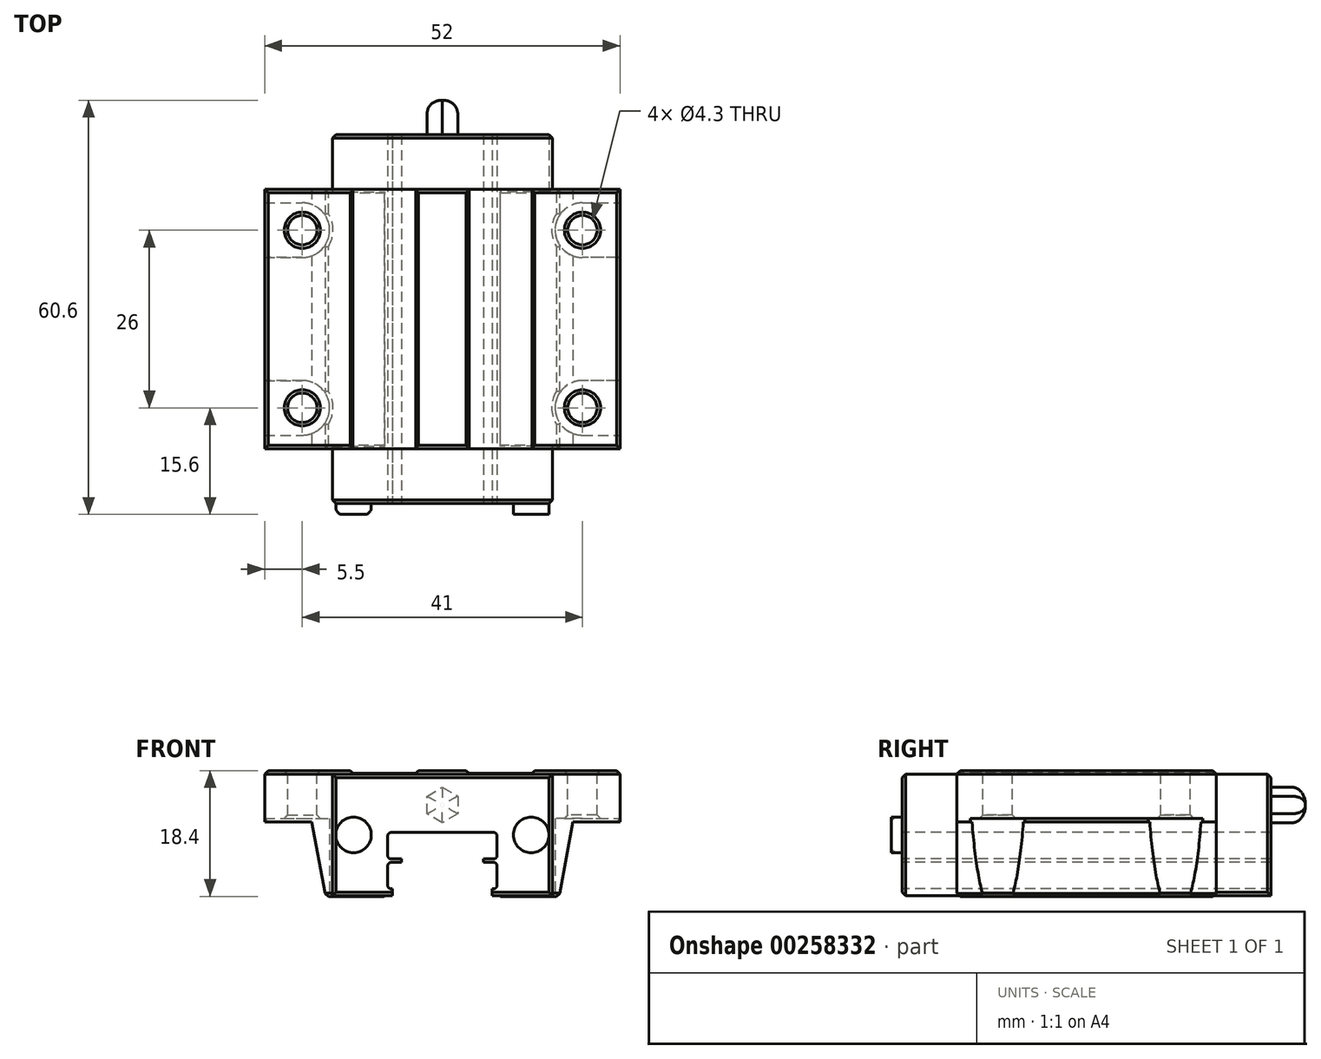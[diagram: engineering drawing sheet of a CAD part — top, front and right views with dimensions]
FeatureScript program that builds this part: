
annotation { "Feature Type Name" : "Feature", "Feature Type Description" : "" }
export const myFeature = defineFeature(function(context is Context, id is Id, definition is map)
    precondition{}
    {
        {
            var Q0;
            Q0=qCreatedBy(makeId("Front.planeOp"),FACE);
            var sketch = newSketch(context, id + "F0", { "sketchPlane" : qUnion([Q0])});
            skLineSegment(sketch, "E0", {"start": v(0, 7.25) * mm, "end": v(0, -7.25) * mm, "construction": true});
            skLineSegment(sketch, "E1", {"start": v(0, -7.25) * mm, "end": v(-7.5, -7.25) * mm});
            skLineSegment(sketch, "E2", {"start": v(-7.5, -7.25) * mm, "end": v(-7.5, -4.13) * mm});
            skLineSegment(sketch, "E3", {"start": v(-7.5, -4.13) * mm, "end": v(-7.5, -4.13) * mm});
            skLineSegment(sketch, "E4", {"start": v(-6.8, -3.43) * mm, "end": v(-6.8, -0.7) * mm});
            skLineSegment(sketch, "E5", {"start": v(-7.5, 0) * mm, "end": v(-7.5, 0) * mm});
            skLineSegment(sketch, "E6", {"start": v(-7.5, 0) * mm, "end": v(-7.5, 1.88) * mm});
            skLineSegment(sketch, "E7", {"start": v(-7.5, 1.88) * mm, "end": v(-7.5, 1.88) * mm});
            skLineSegment(sketch, "E8", {"start": v(-6.8, 2.88) * mm, "end": v(-5.5, 2.88) * mm});
            skLineSegment(sketch, "E9", {"start": v(-5.5, 2.88) * mm, "end": v(-5.5, 4.38) * mm});
            skLineSegment(sketch, "E10", {"start": v(-5.5, 4.38) * mm, "end": v(-6.8, 4.38) * mm});
            skLineSegment(sketch, "E11", {"start": v(-6.8, 4.38) * mm, "end": v(-6.8, 4.68) * mm});
            skLineSegment(sketch, "E12", {"start": v(-7.5, 5.38) * mm, "end": v(-7.5, 5.38) * mm});
            skLineSegment(sketch, "E13", {"start": v(-7.5, 5.38) * mm, "end": v(-7.5, 7.25) * mm});
            skLineSegment(sketch, "E14", {"start": v(-7.5, 7.25) * mm, "end": v(0, 7.25) * mm});
            skLineSegment(sketch, "E15", {"start": v(-6.8, 2.58) * mm, "end": v(-6.8, 2.87) * mm});
            skPoint(sketch, "E16.visualSharp", {"position": v(-6.8, -4.13) * mm});
            skArc(sketch, "E16.filletArc", {"start": v(-7.5, -4.13) * mm, "mid": v(-7, -3.92) * mm, "end": v(-6.8, -3.43) * mm});
            skPoint(sketch, "E17.visualSharp", {"position": v(-6.8, 0) * mm});
            skArc(sketch, "E17.filletArc", {"start": v(-6.8, -0.7) * mm, "mid": v(-7, -0.2) * mm, "end": v(-7.5, 0) * mm});
            skPoint(sketch, "E18.visualSharp", {"position": v(-6.8, 1.88) * mm});
            skArc(sketch, "E18.filletArc", {"start": v(-7.5, 1.88) * mm, "mid": v(-7, 2.08) * mm, "end": v(-6.8, 2.58) * mm});
            skPoint(sketch, "E19.visualSharp", {"position": v(-6.8, 5.38) * mm});
            skArc(sketch, "E19.filletArc", {"start": v(-6.8, 4.68) * mm, "mid": v(-7, 5.17) * mm, "end": v(-7.5, 5.38) * mm});
            skLineSegment(sketch, "E20.MirrorCS", {"start": v(6.8, 2.58) * mm, "end": v(6.8, 2.87) * mm});
            skLineSegment(sketch, "E21.MirrorCS", {"start": v(6.8, 4.38) * mm, "end": v(6.8, 4.68) * mm});
            skArc(sketch, "E22.MirrorCS", {"start": v(6.8, 4.68) * mm, "mid": v(7, 5.17) * mm, "end": v(7.5, 5.38) * mm});
            skArc(sketch, "E23.MirrorCS", {"start": v(7.5, 1.88) * mm, "mid": v(7, 2.08) * mm, "end": v(6.8, 2.58) * mm});
            skArc(sketch, "E24.MirrorCS", {"start": v(7.5, -4.13) * mm, "mid": v(7, -3.92) * mm, "end": v(6.8, -3.43) * mm});
            skArc(sketch, "E25.MirrorCS", {"start": v(6.8, -0.7) * mm, "mid": v(7, -0.2) * mm, "end": v(7.5, 0) * mm});
            skLineSegment(sketch, "E26.MirrorCS", {"start": v(7.5, 0) * mm, "end": v(7.5, 0) * mm});
            skLineSegment(sketch, "E27.MirrorCS", {"start": v(7.5, -7.25) * mm, "end": v(7.5, -4.13) * mm});
            skPoint(sketch, "E28.MirrorP", {"position": v(6.8, 0) * mm});
            skPoint(sketch, "E29.MirrorP", {"position": v(6.8, 5.38) * mm});
            skPoint(sketch, "E30.MirrorP", {"position": v(6.8, 1.88) * mm});
            skLineSegment(sketch, "E31.MirrorCS", {"start": v(7.5, -4.13) * mm, "end": v(7.5, -4.13) * mm});
            skLineSegment(sketch, "E32.MirrorCS", {"start": v(7.5, 1.88) * mm, "end": v(7.5, 1.88) * mm});
            skLineSegment(sketch, "E33.MirrorCS", {"start": v(7.5, 5.38) * mm, "end": v(7.5, 5.38) * mm});
            skLineSegment(sketch, "E34.MirrorCS", {"start": v(7.5, 5.38) * mm, "end": v(7.5, 7.25) * mm});
            skLineSegment(sketch, "E35.MirrorCS", {"start": v(5.5, 4.38) * mm, "end": v(6.8, 4.38) * mm});
            skLineSegment(sketch, "E36.MirrorCS", {"start": v(6.8, -3.43) * mm, "end": v(6.8, -0.7) * mm});
            skPoint(sketch, "E37.MirrorP", {"position": v(6.8, -4.13) * mm});
            skLineSegment(sketch, "E38.MirrorCS", {"start": v(6.8, 2.88) * mm, "end": v(5.5, 2.88) * mm});
            skLineSegment(sketch, "E39.MirrorCS", {"start": v(7.5, 0) * mm, "end": v(7.5, 1.88) * mm});
            skLineSegment(sketch, "E40.MirrorCS", {"start": v(5.5, 2.88) * mm, "end": v(5.5, 4.38) * mm});
            skLineSegment(sketch, "E41.MirrorCS", {"start": v(7.5, 7.25) * mm, "end": v(0, 7.25) * mm});
            skLineSegment(sketch, "E42.MirrorCS", {"start": v(0, -7.25) * mm, "end": v(7.5, -7.25) * mm});
            skSolve(sketch);
        }
        {
            var Q0;
            Q0=qCreatedBy(makeId("Front.planeOp"),FACE);
            var sketch = newSketch(context, id + "F1", { "sketchPlane" : qUnion([Q0])});
            skLineSegment(sketch, "E43", {"start": v(-16.1, 16.3) * mm, "end": v(-16.1, -1.5) * mm});
            skLineSegment(sketch, "E44", {"start": v(-16.1, -1.5) * mm, "end": v(-7.3, -1.5) * mm});
            skLineSegment(sketch, "E45", {"start": v(-7.3, -1.5) * mm, "end": v(-7.3, -0.5) * mm});
            skLineSegment(sketch, "E46", {"start": v(-7.3, -0.5) * mm, "end": v(-7.5, -0.5) * mm});
            skLineSegment(sketch, "E47", {"start": v(-8, 0) * mm, "end": v(-8, 2.88) * mm});
            skLineSegment(sketch, "E48", {"start": v(-7.5, 3.38) * mm, "end": v(-6, 3.38) * mm});
            skLineSegment(sketch, "E49", {"start": v(-6, 3.38) * mm, "end": v(-6, 3.88) * mm});
            skLineSegment(sketch, "E50", {"start": v(-6, 3.88) * mm, "end": v(-7.5, 3.88) * mm});
            skLineSegment(sketch, "E51", {"start": v(-8, 4.38) * mm, "end": v(-8, 7.25) * mm});
            skLineSegment(sketch, "E52", {"start": v(-7.5, 7.75) * mm, "end": v(0, 7.75) * mm});
            skLineSegment(sketch, "E53", {"start": v(-16.1, 16.3) * mm, "end": v(0, 16.3) * mm});
            skLineSegment(sketch, "E54", {"start": v(0, 16.3) * mm, "end": v(0, 0) * mm, "construction": true});
            skPoint(sketch, "E55.visualSharp", {"position": v(-8, 7.75) * mm});
            skArc(sketch, "E55.filletArc", {"start": v(-7.5, 7.75) * mm, "mid": v(-7.85, 7.6) * mm, "end": v(-8, 7.25) * mm});
            skPoint(sketch, "E56.visualSharp", {"position": v(-8, 3.88) * mm});
            skArc(sketch, "E56.filletArc", {"start": v(-8, 4.38) * mm, "mid": v(-7.85, 4.02) * mm, "end": v(-7.5, 3.88) * mm});
            skPoint(sketch, "E57.visualSharp", {"position": v(-8, 3.38) * mm});
            skArc(sketch, "E57.filletArc", {"start": v(-7.5, 3.38) * mm, "mid": v(-7.85, 3.23) * mm, "end": v(-8, 2.88) * mm});
            skPoint(sketch, "E58.visualSharp", {"position": v(-8, -0.5) * mm});
            skArc(sketch, "E58.filletArc", {"start": v(-8, 0) * mm, "mid": v(-7.85, -0.35) * mm, "end": v(-7.5, -0.5) * mm});
            skArc(sketch, "E59.MirrorCS", {"start": v(7.5, 7.75) * mm, "mid": v(7.85, 7.6) * mm, "end": v(8, 7.25) * mm});
            skArc(sketch, "E60.MirrorCS", {"start": v(7.5, 3.38) * mm, "mid": v(7.85, 3.23) * mm, "end": v(8, 2.88) * mm});
            skArc(sketch, "E61.MirrorCS", {"start": v(8, 0) * mm, "mid": v(7.85, -0.35) * mm, "end": v(7.5, -0.5) * mm});
            skLineSegment(sketch, "E62.MirrorCS", {"start": v(7.3, -0.5) * mm, "end": v(7.5, -0.5) * mm});
            skArc(sketch, "E63.MirrorCS", {"start": v(8, 4.38) * mm, "mid": v(7.85, 4.02) * mm, "end": v(7.5, 3.88) * mm});
            skLineSegment(sketch, "E64.MirrorCS", {"start": v(6, 3.88) * mm, "end": v(7.5, 3.88) * mm});
            skLineSegment(sketch, "E65.MirrorCS", {"start": v(8, 4.38) * mm, "end": v(8, 7.25) * mm});
            skLineSegment(sketch, "E66.MirrorCS", {"start": v(7.5, 3.38) * mm, "end": v(6, 3.38) * mm});
            skLineSegment(sketch, "E67.MirrorCS", {"start": v(7.3, -1.5) * mm, "end": v(7.3, -0.5) * mm});
            skLineSegment(sketch, "E68.MirrorCS", {"start": v(8, 0) * mm, "end": v(8, 2.88) * mm});
            skLineSegment(sketch, "E69.MirrorCS", {"start": v(6, 3.38) * mm, "end": v(6, 3.88) * mm});
            skPoint(sketch, "E70.MirrorP", {"position": v(8, 3.38) * mm});
            skPoint(sketch, "E71.MirrorP", {"position": v(8, 3.88) * mm});
            skLineSegment(sketch, "E72.MirrorCS", {"start": v(7.5, 7.75) * mm, "end": v(0, 7.75) * mm});
            skPoint(sketch, "E73.MirrorP", {"position": v(8, -0.5) * mm});
            skLineSegment(sketch, "E74.MirrorCS", {"start": v(16.1, 16.3) * mm, "end": v(0, 16.3) * mm});
            skLineSegment(sketch, "E75.MirrorCS", {"start": v(16.1, 16.3) * mm, "end": v(16.1, -1.5) * mm});
            skLineSegment(sketch, "E76.MirrorCS", {"start": v(16.1, -1.5) * mm, "end": v(7.3, -1.5) * mm});
            skPoint(sketch, "E77.MirrorP", {"position": v(8, 7.75) * mm});
            skSolve(sketch);
        }
        {
            var Q0;
            Q0=qSketchRegion(id+"F1",true);
            extrude(context, id + "F2", {"entities" : qUnion([Q0]), "oppositeDirection" : true, "depth" : 54 * mm});
        }
        {
            var Q0;
            Q0=qCreatedBy(makeId("Front.planeOp"),FACE);
            cPlane(context, id + "F3", {"entities" : qUnion([Q0]), "cplaneType" : CPlaneType.OFFSET, "offset" : 8 * mm, "oppositeDirection" : true, "width" : 150 * mm, "height" : 150 * mm});
        }
        {
            var Q0;
            Q0=qCreatedBy(id+"F3.planeOp",FACE);
            var sketch = newSketch(context, id + "F4", { "sketchPlane" : qUnion([Q0])});
            skLineSegment(sketch, "E78", {"start": v(-8, -1.6) * mm, "end": v(-17.1, -1.6) * mm});
            skLineSegment(sketch, "E79", {"start": v(-17.1, -1.6) * mm, "end": v(-19.1, 9.3) * mm});
            skLineSegment(sketch, "E80", {"start": v(-19.1, 9.3) * mm, "end": v(-26, 9.3) * mm});
            skLineSegment(sketch, "E81", {"start": v(-26, 9.3) * mm, "end": v(-26, 16.8) * mm});
            skLineSegment(sketch, "E82", {"start": v(0, 16.8) * mm, "end": v(0, 0) * mm, "construction": true});
            skLineSegment(sketch, "E83", {"start": v(-26, 16.8) * mm, "end": v(-13, 16.8) * mm});
            skLineSegment(sketch, "E84", {"start": v(-13, 16.8) * mm, "end": v(-13, 16.4) * mm});
            skLineSegment(sketch, "E85", {"start": v(-13, 16.4) * mm, "end": v(-4, 16.4) * mm});
            skLineSegment(sketch, "E86", {"start": v(-4, 16.4) * mm, "end": v(-4, 16.8) * mm});
            skLineSegment(sketch, "E87", {"start": v(-4, 16.8) * mm, "end": v(0, 16.8) * mm});
            skLineSegment(sketch, "E88", {"start": v(-8, -1.6) * mm, "end": v(-8, 7.75) * mm});
            skLineSegment(sketch, "E89", {"start": v(-8, 7.75) * mm, "end": v(0, 7.75) * mm});
            skLineSegment(sketch, "E90.MirrorCS", {"start": v(4, 16.4) * mm, "end": v(4, 16.8) * mm});
            skLineSegment(sketch, "E91.MirrorCS", {"start": v(13, 16.8) * mm, "end": v(13, 16.4) * mm});
            skLineSegment(sketch, "E92.MirrorCS", {"start": v(8, -1.6) * mm, "end": v(8, 7.75) * mm});
            skLineSegment(sketch, "E93.MirrorCS", {"start": v(4, 16.8) * mm, "end": v(0, 16.8) * mm});
            skLineSegment(sketch, "E94.MirrorCS", {"start": v(26, 16.8) * mm, "end": v(13, 16.8) * mm});
            skLineSegment(sketch, "E95.MirrorCS", {"start": v(26, 9.3) * mm, "end": v(26, 16.8) * mm});
            skLineSegment(sketch, "E96.MirrorCS", {"start": v(8, -1.6) * mm, "end": v(17.1, -1.6) * mm});
            skLineSegment(sketch, "E97.MirrorCS", {"start": v(17.1, -1.6) * mm, "end": v(19.1, 9.3) * mm});
            skLineSegment(sketch, "E98.MirrorCS", {"start": v(8, 7.75) * mm, "end": v(0, 7.75) * mm});
            skLineSegment(sketch, "E99.MirrorCS", {"start": v(19.1, 9.3) * mm, "end": v(26, 9.3) * mm});
            skLineSegment(sketch, "E100.MirrorCS", {"start": v(13, 16.4) * mm, "end": v(4, 16.4) * mm});
            skSolve(sketch);
        }
        {
            var Q0;
            Q0=qSketchRegion(id+"F4",true);
            extrude(context, id + "F5", {"entities" : qUnion([Q0]), "operationType" : NewBodyOperationType.ADD, "oppositeDirection" : true, "depth" : 38 * mm});
        }
        {
            var Q0;
            Q0=makeQuery(id+"F5.opExtrude","SWEPT_FACE",FACE,{"disambiguationData":[OSD([sQuery(id+"F4.wireOp",EDGE,"E83")])]});
            var sketch = newSketch(context, id + "F6", { "sketchPlane" : qUnion([Q0])});
            skCircle(sketch, "E101", {"center": v(-20.5, 40) * mm, "radius": 2.15 * mm});
            skCircle(sketch, "E102", {"center": v(-20.5, 14) * mm, "radius": 2.15 * mm});
            skLineSegment(sketch, "E103", {"start": v(-26, 27) * mm, "end": v(-13, 27) * mm, "construction": true});
            skCircle(sketch, "E104.MirrorC", {"center": v(20.5, 40) * mm, "radius": 2.15 * mm});
            skCircle(sketch, "E105.MirrorC", {"center": v(20.5, 14) * mm, "radius": 2.15 * mm});
            skSolve(sketch);
        }
        {
            var Q0;
            Q0=qSketchRegion(id+"F6",true);
            extrude(context, id + "F7", {"entities" : qUnion([Q0]), "operationType" : NewBodyOperationType.REMOVE, "endBound" : BoundingType.THROUGH_ALL, "oppositeDirection" : true, "depth" : 25 * mm});
        }
        {
            var Q0;
            Q0=makeQuery(id+"F5.opExtrude","SWEPT_FACE",FACE,{"disambiguationData":[OSD([sQuery(id+"F4.wireOp",EDGE,"E80")])]});
            var sketch = newSketch(context, id + "F8", { "sketchPlane" : qUnion([Q0])});
            skArc(sketch, "E106", {"start": v(-20.5, -18) * mm, "mid": v(-16.5, -14) * mm, "end": v(-20.5, -10) * mm});
            skLineSegment(sketch, "E107", {"start": v(-26, -27) * mm, "end": v(-19.1, -27) * mm, "construction": true});
            skLineSegment(sketch, "E108", {"start": v(-20.5, -10) * mm, "end": v(-26, -10) * mm});
            skLineSegment(sketch, "E109", {"start": v(-26, -10) * mm, "end": v(-26, -18) * mm});
            skLineSegment(sketch, "E110", {"start": v(-26, -18) * mm, "end": v(-20.5, -18) * mm});
            skLineSegment(sketch, "E111.MirrorCS", {"start": v(-26, -36) * mm, "end": v(-20.5, -36) * mm});
            skLineSegment(sketch, "E112.MirrorCS", {"start": v(-26, -44) * mm, "end": v(-26, -36) * mm});
            skLineSegment(sketch, "E113.MirrorCS", {"start": v(-20.5, -44) * mm, "end": v(-26, -44) * mm});
            skArc(sketch, "E114.MirrorCS", {"start": v(-20.5, -36) * mm, "mid": v(-16.5, -40) * mm, "end": v(-20.5, -44) * mm});
            skArc(sketch, "E115.MirrorCS", {"start": v(20.5, -18) * mm, "mid": v(16.5, -14) * mm, "end": v(20.5, -10) * mm});
            skLineSegment(sketch, "E116.MirrorCS", {"start": v(26, -18) * mm, "end": v(20.5, -18) * mm});
            skLineSegment(sketch, "E117.MirrorCS", {"start": v(26, -10) * mm, "end": v(26, -18) * mm});
            skLineSegment(sketch, "E118.MirrorCS", {"start": v(20.5, -10) * mm, "end": v(26, -10) * mm});
            skLineSegment(sketch, "E119.MirrorCS", {"start": v(26, -36) * mm, "end": v(20.5, -36) * mm});
            skArc(sketch, "E120.MirrorCS", {"start": v(20.5, -36) * mm, "mid": v(16.5, -40) * mm, "end": v(20.5, -44) * mm});
            skLineSegment(sketch, "E121.MirrorCS", {"start": v(20.5, -44) * mm, "end": v(26, -44) * mm});
            skLineSegment(sketch, "E122.MirrorCS", {"start": v(26, -44) * mm, "end": v(26, -36) * mm});
            skSolve(sketch);
        }
        {
            var Q0;
            Q0=qSketchRegion(id+"F8",true);
            extrude(context, id + "F9", {"entities" : qUnion([Q0]), "operationType" : NewBodyOperationType.REMOVE, "oppositeDirection" : true, "depth" : 0.5 * mm, "hasSecondDirection" : true, "secondDirectionBound" : BoundingType.THROUGH_ALL, "secondDirectionOppositeDirection" : false, "secondDirectionDepth" : 25 * mm});
        }
        {
            var Q0;
            Q0=makeQuery(id+"F5.opExtrude","SWEPT_FACE",FACE,{"disambiguationData":[OSD([sQuery(id+"F4.wireOp",EDGE,"E78")])]});
            var Q1;
            Q1=makeQuery(id+"F5.opExtrude","SWEPT_FACE",FACE,{"disambiguationData":[OSD([sQuery(id+"F4.wireOp",EDGE,"E96.MirrorCS")])]});
            var Q2;
            Q2=makeQuery(id+"F7.boolean.opBoolean","COPY",FACE,{"derivedFrom":makeQuery(id+"F7.opExtrude","SWEPT_FACE",FACE,{"disambiguationData":[OSD([sQuery(id+"F6.wireOp",EDGE,"E101")])]})});
            var Q3;
            Q3=makeQuery(id+"F7.boolean.opBoolean","COPY",FACE,{"derivedFrom":makeQuery(id+"F7.opExtrude","SWEPT_FACE",FACE,{"disambiguationData":[OSD([sQuery(id+"F6.wireOp",EDGE,"E102")])]})});
            var Q4;
            Q4=makeQuery(id+"F7.boolean.opBoolean","COPY",FACE,{"derivedFrom":makeQuery(id+"F7.opExtrude","SWEPT_FACE",FACE,{"disambiguationData":[OSD([sQuery(id+"F6.wireOp",EDGE,"E105.MirrorC")])]})});
            var Q5;
            Q5=makeQuery(id+"F7.boolean.opBoolean","COPY",FACE,{"derivedFrom":makeQuery(id+"F7.opExtrude","SWEPT_FACE",FACE,{"disambiguationData":[OSD([sQuery(id+"F6.wireOp",EDGE,"E104.MirrorC")])]})});
            var Q6;
            Q6=makeQuery(id+"F5.opExtrude","SWEPT_FACE",FACE,{"disambiguationData":[OSD([sQuery(id+"F4.wireOp",EDGE,"E87"),sQuery(id+"F4.wireOp",EDGE,"E93.MirrorCS")])]});
            var Q7;
            Q7=makeQuery(id+"F5.opExtrude","SWEPT_FACE",FACE,{"disambiguationData":[OSD([sQuery(id+"F4.wireOp",EDGE,"E94.MirrorCS")])]});
            var Q8;
            Q8=makeQuery(id+"F5.opExtrude","SWEPT_FACE",FACE,{"disambiguationData":[OSD([sQuery(id+"F4.wireOp",EDGE,"E83")])]});
            chamfer(context, id + "F10", {"entities" : qUnion([Q0, Q1, Q2, Q3, Q4, Q5, Q6, Q7, Q8]), "width" : 0.5 * mm, "tangentPropagation" : true});
        }
        {
            var Q0;
            {var subQ0=sQuery(id+"F4.wireOp",EDGE,"E95.MirrorCS");var subQ1=sQuery(id+"F4.wireOp",EDGE,"E99.MirrorCS");Q0=makeQuery(id+"F9.boolean.opBoolean","SPLIT",EDGE,{"disambiguationData":[TD([makeQuery(id+"F9.opExtrude","SWEPT_FACE",FACE,{"disambiguationData":[OSD([sQuery(id+"F8.wireOp",EDGE,"E116.MirrorCS")])]})])],"derivedFrom":makeQuery(id+"F5.opExtrude","SWEPT_EDGE",EDGE,{"disambiguationData":[OSD([subQ0,subQ1])]})});}
            var Q1;
            {var subQ0=sQuery(id+"F1.wireOp",EDGE,"E76.MirrorCS");var subQ1=sQuery(id+"F1.wireOp",EDGE,"E75.MirrorCS");Q1=makeQuery(id+"F5.boolean.opBoolean","SPLIT",EDGE,{"disambiguationData":[TD([makeQuery(id+"F5.opExtrude","CAP_FACE",FACE,{"disambiguationData":[OSD([sQuery(id+"F4.wireOp",EDGE,"E78"),sQuery(id+"F4.wireOp",EDGE,"E79"),sQuery(id+"F4.wireOp",EDGE,"E80"),sQuery(id+"F4.wireOp",EDGE,"E81"),sQuery(id+"F4.wireOp",EDGE,"E83"),sQuery(id+"F4.wireOp",EDGE,"E84"),sQuery(id+"F4.wireOp",EDGE,"E85"),sQuery(id+"F4.wireOp",EDGE,"E86"),sQuery(id+"F4.wireOp",EDGE,"E87"),sQuery(id+"F4.wireOp",EDGE,"E88"),sQuery(id+"F4.wireOp",EDGE,"E89"),sQuery(id+"F4.wireOp",EDGE,"E90.MirrorCS"),sQuery(id+"F4.wireOp",EDGE,"E91.MirrorCS"),sQuery(id+"F4.wireOp",EDGE,"E92.MirrorCS"),sQuery(id+"F4.wireOp",EDGE,"E93.MirrorCS"),sQuery(id+"F4.wireOp",EDGE,"E94.MirrorCS"),sQuery(id+"F4.wireOp",EDGE,"E95.MirrorCS"),sQuery(id+"F4.wireOp",EDGE,"E96.MirrorCS"),sQuery(id+"F4.wireOp",EDGE,"E97.MirrorCS"),sQuery(id+"F4.wireOp",EDGE,"E98.MirrorCS"),sQuery(id+"F4.wireOp",EDGE,"E99.MirrorCS"),sQuery(id+"F4.wireOp",EDGE,"E100.MirrorCS")])],"isStart":false})])],"derivedFrom":makeQuery(id+"F2.opExtrude","SWEPT_EDGE",EDGE,{"disambiguationData":[OSD([subQ1,subQ0])]})});}
            var Q2;
            Q2=makeQuery(id+"F2.opExtrude","CAP_EDGE",EDGE,{"disambiguationData":[OSD([sQuery(id+"F1.wireOp",EDGE,"E75.MirrorCS")])],"isStart":false});
            var Q3;
            Q3=makeQuery(id+"F2.opExtrude","CAP_EDGE",EDGE,{"disambiguationData":[OSD([sQuery(id+"F1.wireOp",EDGE,"E53"),sQuery(id+"F1.wireOp",EDGE,"E74.MirrorCS")])],"isStart":false});
            var Q4;
            Q4=makeQuery(id+"F2.opExtrude","CAP_EDGE",EDGE,{"disambiguationData":[OSD([sQuery(id+"F1.wireOp",EDGE,"E43")])],"isStart":false});
            var Q5;
            Q5=makeQuery(id+"F2.opExtrude","CAP_EDGE",EDGE,{"disambiguationData":[OSD([sQuery(id+"F1.wireOp",EDGE,"E44")])],"isStart":false});
            var Q6;
            Q6=makeQuery(id+"F2.opExtrude","CAP_EDGE",EDGE,{"disambiguationData":[OSD([sQuery(id+"F1.wireOp",EDGE,"E43")])],"isStart":true});
            var Q7;
            Q7=makeQuery(id+"F2.opExtrude","CAP_EDGE",EDGE,{"disambiguationData":[OSD([sQuery(id+"F1.wireOp",EDGE,"E44")])],"isStart":true});
            var Q8;
            Q8=makeQuery(id+"F2.opExtrude","CAP_EDGE",EDGE,{"disambiguationData":[OSD([sQuery(id+"F1.wireOp",EDGE,"E76.MirrorCS")])],"isStart":true});
            var Q9;
            Q9=makeQuery(id+"F2.opExtrude","CAP_EDGE",EDGE,{"disambiguationData":[OSD([sQuery(id+"F1.wireOp",EDGE,"E75.MirrorCS")])],"isStart":true});
            var Q10;
            Q10=makeQuery(id+"F2.opExtrude","CAP_EDGE",EDGE,{"disambiguationData":[OSD([sQuery(id+"F1.wireOp",EDGE,"E53"),sQuery(id+"F1.wireOp",EDGE,"E74.MirrorCS")])],"isStart":true});
            var Q11;
            {var subQ0=sQuery(id+"F4.wireOp",EDGE,"E80");var subQ1=sQuery(id+"F4.wireOp",EDGE,"E81");Q11=makeQuery(id+"F9.boolean.opBoolean","SPLIT",EDGE,{"disambiguationData":[TD([makeQuery(id+"F9.opExtrude","SWEPT_FACE",FACE,{"disambiguationData":[OSD([sQuery(id+"F8.wireOp",EDGE,"E110")])]})])],"derivedFrom":makeQuery(id+"F5.opExtrude","SWEPT_EDGE",EDGE,{"disambiguationData":[OSD([subQ0,subQ1])]})});}
            chamfer(context, id + "F11", {"entities" : qUnion([Q0, Q1, Q2, Q3, Q4, Q5, Q6, Q7, Q8, Q9, Q10, Q11]), "width" : 0.5 * mm, "tangentPropagation" : true});
        }
        {
            var Q0;
            Q0=makeQuery(id+"F2.opExtrude","CAP_FACE",FACE,{"disambiguationData":[OSD([sQuery(id+"F1.wireOp",EDGE,"E43"),sQuery(id+"F1.wireOp",EDGE,"E44"),sQuery(id+"F1.wireOp",EDGE,"E45"),sQuery(id+"F1.wireOp",EDGE,"E46"),sQuery(id+"F1.wireOp",EDGE,"E47"),sQuery(id+"F1.wireOp",EDGE,"E48"),sQuery(id+"F1.wireOp",EDGE,"E49"),sQuery(id+"F1.wireOp",EDGE,"E50"),sQuery(id+"F1.wireOp",EDGE,"E51"),sQuery(id+"F1.wireOp",EDGE,"E52"),sQuery(id+"F1.wireOp",EDGE,"E53"),sQuery(id+"F1.wireOp",EDGE,"E55.filletArc"),sQuery(id+"F1.wireOp",EDGE,"E56.filletArc"),sQuery(id+"F1.wireOp",EDGE,"E57.filletArc"),sQuery(id+"F1.wireOp",EDGE,"E58.filletArc"),sQuery(id+"F1.wireOp",EDGE,"E59.MirrorCS"),sQuery(id+"F1.wireOp",EDGE,"E60.MirrorCS"),sQuery(id+"F1.wireOp",EDGE,"E61.MirrorCS"),sQuery(id+"F1.wireOp",EDGE,"E62.MirrorCS"),sQuery(id+"F1.wireOp",EDGE,"E63.MirrorCS"),sQuery(id+"F1.wireOp",EDGE,"E64.MirrorCS"),sQuery(id+"F1.wireOp",EDGE,"E65.MirrorCS"),sQuery(id+"F1.wireOp",EDGE,"E66.MirrorCS"),sQuery(id+"F1.wireOp",EDGE,"E67.MirrorCS"),sQuery(id+"F1.wireOp",EDGE,"E68.MirrorCS"),sQuery(id+"F1.wireOp",EDGE,"E69.MirrorCS"),sQuery(id+"F1.wireOp",EDGE,"E72.MirrorCS"),sQuery(id+"F1.wireOp",EDGE,"E74.MirrorCS"),sQuery(id+"F1.wireOp",EDGE,"E75.MirrorCS"),sQuery(id+"F1.wireOp",EDGE,"E76.MirrorCS")])],"isStart":true});
            var sketch = newSketch(context, id + "F12", { "sketchPlane" : qUnion([Q0])});
            skLineSegment(sketch, "E123", {"start": v(-15.6, 7.4) * mm, "end": v(15.6, 7.4) * mm, "construction": true});
            skCircle(sketch, "E124", {"center": v(-13, 7.4) * mm, "radius": 2.6 * mm});
            skLineSegment(sketch, "E125", {"start": v(0, 0) * mm, "end": v(0, 15.8) * mm, "construction": true});
            skCircle(sketch, "E126", {"center": v(13, 7.4) * mm, "radius": 2.6 * mm});
            skSolve(sketch);
        }
        {
            var Q0;
            Q0=qSketchRegion(id+"F12",true);
            extrude(context, id + "F13", {"entities" : qUnion([Q0]), "operationType" : NewBodyOperationType.ADD, "depth" : 1.6 * mm});
        }
        {
            var Q0;
            Q0=makeQuery(id+"F2.opExtrude","CAP_FACE",FACE,{"disambiguationData":[OSD([sQuery(id+"F1.wireOp",EDGE,"E43"),sQuery(id+"F1.wireOp",EDGE,"E44"),sQuery(id+"F1.wireOp",EDGE,"E45"),sQuery(id+"F1.wireOp",EDGE,"E46"),sQuery(id+"F1.wireOp",EDGE,"E47"),sQuery(id+"F1.wireOp",EDGE,"E48"),sQuery(id+"F1.wireOp",EDGE,"E49"),sQuery(id+"F1.wireOp",EDGE,"E50"),sQuery(id+"F1.wireOp",EDGE,"E51"),sQuery(id+"F1.wireOp",EDGE,"E52"),sQuery(id+"F1.wireOp",EDGE,"E53"),sQuery(id+"F1.wireOp",EDGE,"E55.filletArc"),sQuery(id+"F1.wireOp",EDGE,"E56.filletArc"),sQuery(id+"F1.wireOp",EDGE,"E57.filletArc"),sQuery(id+"F1.wireOp",EDGE,"E58.filletArc"),sQuery(id+"F1.wireOp",EDGE,"E59.MirrorCS"),sQuery(id+"F1.wireOp",EDGE,"E60.MirrorCS"),sQuery(id+"F1.wireOp",EDGE,"E61.MirrorCS"),sQuery(id+"F1.wireOp",EDGE,"E62.MirrorCS"),sQuery(id+"F1.wireOp",EDGE,"E63.MirrorCS"),sQuery(id+"F1.wireOp",EDGE,"E64.MirrorCS"),sQuery(id+"F1.wireOp",EDGE,"E65.MirrorCS"),sQuery(id+"F1.wireOp",EDGE,"E66.MirrorCS"),sQuery(id+"F1.wireOp",EDGE,"E67.MirrorCS"),sQuery(id+"F1.wireOp",EDGE,"E68.MirrorCS"),sQuery(id+"F1.wireOp",EDGE,"E69.MirrorCS"),sQuery(id+"F1.wireOp",EDGE,"E72.MirrorCS"),sQuery(id+"F1.wireOp",EDGE,"E74.MirrorCS"),sQuery(id+"F1.wireOp",EDGE,"E75.MirrorCS"),sQuery(id+"F1.wireOp",EDGE,"E76.MirrorCS")])],"isStart":false});
            var sketch = newSketch(context, id + "F14", { "sketchPlane" : qUnion([Q0])});
            skLineSegment(sketch, "E127", {"start": v(0, 15.8) * mm, "end": v(0, 7.75) * mm, "construction": true});
            skCircle(sketch, "E128", {"center": v(0, 11.78) * mm, "radius": 2.6 * mm, "construction": true});
            skLineSegment(sketch, "E129", {"start": v(-2.25, 13.07) * mm, "end": v(-2.25, 10.48) * mm});
            skLineSegment(sketch, "E130", {"start": v(-2.25, 10.48) * mm, "end": v(0, 9.18) * mm});
            skLineSegment(sketch, "E131", {"start": v(0, 9.18) * mm, "end": v(2.25, 10.48) * mm});
            skLineSegment(sketch, "E132", {"start": v(2.25, 10.48) * mm, "end": v(2.25, 13.07) * mm});
            skLineSegment(sketch, "E133", {"start": v(2.25, 13.07) * mm, "end": v(0, 14.37) * mm});
            skLineSegment(sketch, "E134", {"start": v(0, 14.37) * mm, "end": v(-2.25, 13.07) * mm});
            skSolve(sketch);
        }
        {
            var Q0;
            Q0=qSketchRegion(id+"F14",true);
            extrude(context, id + "F15", {"entities" : qUnion([Q0]), "operationType" : NewBodyOperationType.ADD, "depth" : 5 * mm});
        }
        {
            var Q0;
            Q0=makeQuery(id+"F15.opExtrude","CAP_FACE",FACE,{"disambiguationData":[OSD([sQuery(id+"F14.wireOp",EDGE,"E129"),sQuery(id+"F14.wireOp",EDGE,"E130"),sQuery(id+"F14.wireOp",EDGE,"E131"),sQuery(id+"F14.wireOp",EDGE,"E132"),sQuery(id+"F14.wireOp",EDGE,"E133"),sQuery(id+"F14.wireOp",EDGE,"E134")])],"isStart":false});
            fillet(context, id + "F16", {"entities" : qUnion([Q0]), "radius" : 2 * mm, "tangentPropagation" : true, "allowEdgeOverflow" : false});
        }
        {
            var Q0;
            Q0=makeQuery(id+"F13.opExtrude","CAP_EDGE",EDGE,{"disambiguationData":[OSD([sQuery(id+"F12.wireOp",EDGE,"E124")])],"isStart":false});
            fillet(context, id + "F17", {"entities" : qUnion([Q0]), "radius" : 1 * mm, "tangentPropagation" : true, "allowEdgeOverflow" : false});
        }
    });
